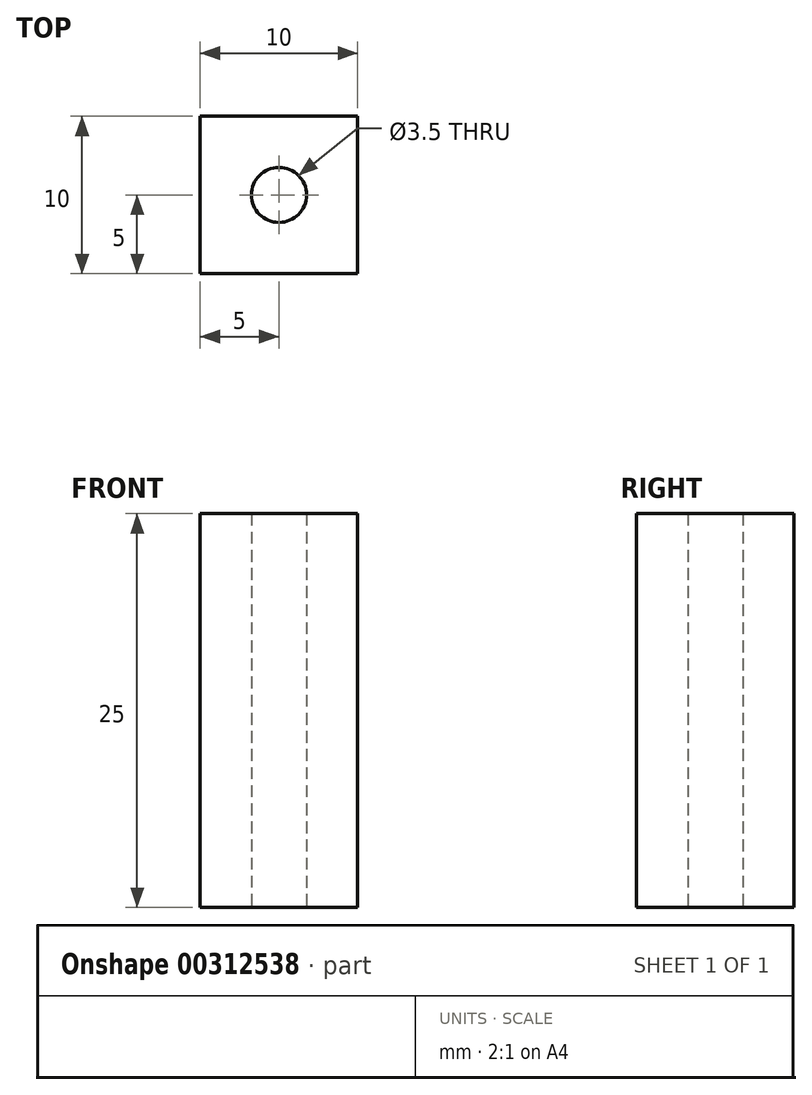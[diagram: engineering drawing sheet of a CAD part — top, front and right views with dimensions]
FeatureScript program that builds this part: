
annotation { "Feature Type Name" : "Feature", "Feature Type Description" : "" }
export const myFeature = defineFeature(function(context is Context, id is Id, definition is map)
    precondition{}
    {
        {
            var Q0;
            Q0=qCreatedBy(makeId("Top.planeOp"),FACE);
            var sketch = newSketch(context, id + "F0", { "sketchPlane" : qUnion([Q0])});
            skCircle(sketch, "E0", {"center": v(0, 0) * mm, "radius": 1.75 * mm});
            skSolve(sketch);
        }
        {
            var Q0;
            Q0=qCreatedBy(makeId("Top.planeOp"),FACE);
            var sketch = newSketch(context, id + "F1", { "sketchPlane" : qUnion([Q0])});
            skLineSegment(sketch, "E1.bottom", {"start": v(-5, 5) * mm, "end": v(5, 5) * mm});
            skLineSegment(sketch, "E1.top", {"start": v(-5, -5) * mm, "end": v(5, -5) * mm});
            skLineSegment(sketch, "E1.left", {"start": v(-5, 5) * mm, "end": v(-5, -5) * mm});
            skLineSegment(sketch, "E1.right", {"start": v(5, 5) * mm, "end": v(5, -5) * mm});
            skSolve(sketch);
        }
        {
            var Q0;
            Q0 = qSketchRegion(id + "F1", true);
            extrude(context, id + "F2", {"entities" : qUnion([Q0]), "depth" : 25 * mm});
        }
        {
            var Q0;
            Q0 = qSketchRegion(id + "F0", true);
            extrude(context, id + "F3", {"entities" : qUnion([Q0]), "operationType" : NewBodyOperationType.REMOVE, "endBound" : BoundingType.UP_TO_NEXT, "depth" : 25 * mm});
        }
    });
